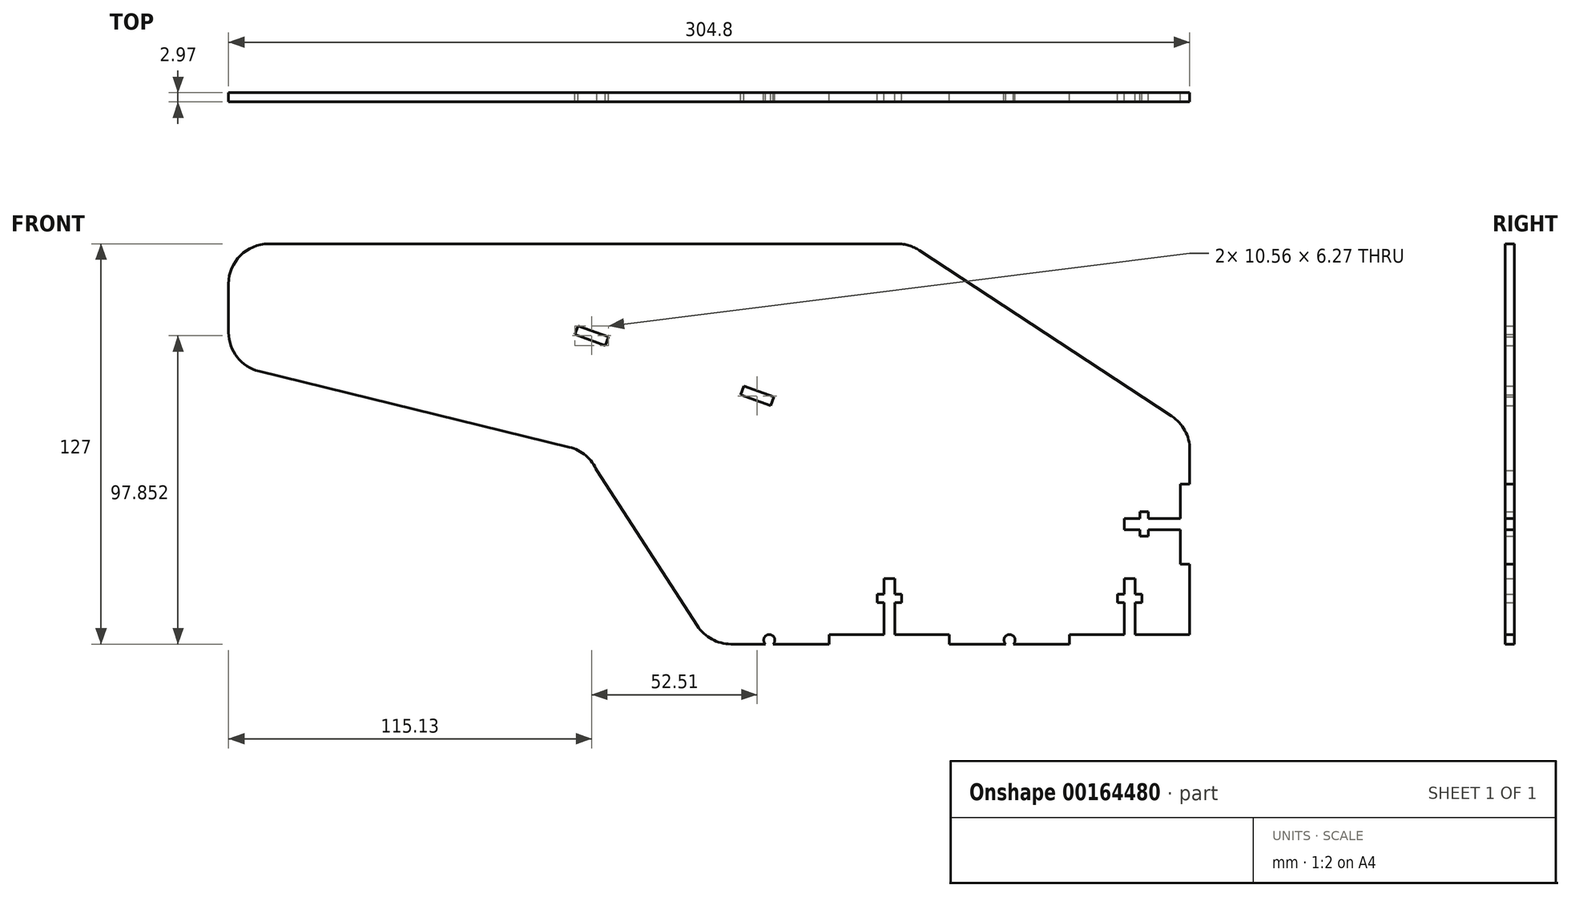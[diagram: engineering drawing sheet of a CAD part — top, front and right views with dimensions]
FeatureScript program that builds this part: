
annotation { "Feature Type Name" : "Feature", "Feature Type Description" : "" }
export const myFeature = defineFeature(function(context is Context, id is Id, definition is map)
    precondition{}
    {
        {
            var Q0;
            Q0=qCreatedBy(makeId("Front.planeOp"),FACE);
            var sketch = newSketch(context, id + "F0", { "sketchPlane" : qUnion([Q0])});
            skLineSegment(sketch, "E0.bottom", {"start": v(152.4, -63.5) * mm, "end": v(17.8, -63.5) * mm});
            skLineSegment(sketch, "E0.top", {"start": v(59.7, 63.5) * mm, "end": v(-139.7, 63.5) * mm});
            skLineSegment(sketch, "E0.left", {"start": v(152.4, -63.5) * mm, "end": v(152.4, -1.77) * mm});
            skLineSegment(sketch, "E0.right", {"start": v(-152.4, 35.37) * mm, "end": v(-152.4, 50.8) * mm});
            skPoint(sketch, "E0.middle", {"position": v(0, 0) * mm});
            skPoint(sketch, "E1", {"position": v(-152.4, 25.4) * mm});
            skPoint(sketch, "E2.orphan", {"position": v(-152.4, -63.5) * mm});
            skLineSegment(sketch, "E3.bottom", {"start": v(38.1, -60.53) * mm, "end": v(55.38, -60.53) * mm});
            skLineSegment(sketch, "E3.top", {"start": v(38.1, -63.5) * mm, "end": v(76.2, -63.5) * mm});
            skLineSegment(sketch, "E3.left", {"start": v(38.1, -60.53) * mm, "end": v(38.1, -63.5) * mm});
            skLineSegment(sketch, "E3.right", {"start": v(76.2, -60.53) * mm, "end": v(76.2, -63.5) * mm});
            skLineSegment(sketch, "E4.bottom", {"start": v(55.38, -42.7) * mm, "end": v(58.92, -42.7) * mm});
            skLineSegment(sketch, "E4.top", {"start": v(55.38, -63.5) * mm, "end": v(58.92, -63.5) * mm});
            skLineSegment(sketch, "E4.left", {"start": v(55.38, -42.7) * mm, "end": v(55.38, -47.73) * mm});
            skLineSegment(sketch, "E4.right", {"start": v(58.92, -42.7) * mm, "end": v(58.92, -47.73) * mm});
            skPoint(sketch, "E5", {"position": v(57.15, -63.5) * mm});
            skLineSegment(sketch, "E6", {"start": v(57.15, -63.5) * mm, "end": v(57.15, -38.1) * mm, "construction": true});
            skPoint(sketch, "E6.endSnap0", {"position": v(57.15, -42.7) * mm});
            skLineSegment(sketch, "E7.bottom", {"start": v(61.04, -50.37) * mm, "end": v(58.92, -50.37) * mm});
            skLineSegment(sketch, "E7.top", {"start": v(61.04, -47.73) * mm, "end": v(58.92, -47.73) * mm});
            skLineSegment(sketch, "E7.left", {"start": v(61.04, -50.37) * mm, "end": v(61.04, -47.73) * mm});
            skLineSegment(sketch, "E7.right", {"start": v(53.26, -50.37) * mm, "end": v(53.26, -47.73) * mm});
            skPoint(sketch, "E7.middle", {"position": v(57.15, -49.05) * mm});
            skLineSegment(sketch, "E8.trimOffspring", {"start": v(58.92, -60.53) * mm, "end": v(76.2, -60.53) * mm});
            skLineSegment(sketch, "E9.trimOffspring", {"start": v(58.92, -50.37) * mm, "end": v(58.92, -60.53) * mm});
            skLineSegment(sketch, "E10.trimOffspring", {"start": v(55.38, -50.37) * mm, "end": v(55.38, -60.53) * mm});
            skLineSegment(sketch, "E11.trimOffspring", {"start": v(55.38, -47.73) * mm, "end": v(53.26, -47.73) * mm});
            skLineSegment(sketch, "E12.trimOffspring", {"start": v(55.38, -50.37) * mm, "end": v(53.26, -50.37) * mm});
            skArc(sketch, "E13", {"start": v(20.3, -63.5) * mm, "mid": v(19.05, -60.45) * mm, "end": v(17.8, -63.5) * mm});
            skLineSegment(sketch, "E14.1.0.0", {"start": v(133.35, -63.5) * mm, "end": v(133.35, -38.1) * mm, "construction": true});
            skLineSegment(sketch, "E14.1.0.1", {"start": v(131.58, -50.37) * mm, "end": v(131.58, -60.53) * mm});
            skPoint(sketch, "E14.1.0.2", {"position": v(133.35, -42.7) * mm});
            skPoint(sketch, "E14.1.0.3", {"position": v(133.35, -63.5) * mm});
            skLineSegment(sketch, "E14.1.0.4", {"start": v(114.3, -60.53) * mm, "end": v(131.58, -60.53) * mm});
            skLineSegment(sketch, "E14.1.0.5", {"start": v(114.3, -63.5) * mm, "end": v(152.4, -63.5) * mm});
            skLineSegment(sketch, "E14.1.0.6", {"start": v(135.12, -50.37) * mm, "end": v(135.12, -60.53) * mm});
            skLineSegment(sketch, "E14.1.0.7", {"start": v(135.12, -60.53) * mm, "end": v(152.4, -60.53) * mm});
            skPoint(sketch, "E14.1.0.8", {"position": v(133.35, -49.05) * mm});
            skArc(sketch, "E14.1.0.9", {"start": v(96.5, -63.5) * mm, "mid": v(95.25, -60.45) * mm, "end": v(94, -63.5) * mm});
            skLineSegment(sketch, "E14.1.0.10", {"start": v(135.12, -42.7) * mm, "end": v(135.12, -47.73) * mm});
            skLineSegment(sketch, "E14.1.0.11", {"start": v(114.3, -60.53) * mm, "end": v(114.3, -63.5) * mm});
            skLineSegment(sketch, "E14.1.0.12", {"start": v(152.4, -60.53) * mm, "end": v(152.4, -63.5) * mm});
            skLineSegment(sketch, "E14.1.0.13", {"start": v(137.24, -47.73) * mm, "end": v(135.12, -47.73) * mm});
            skLineSegment(sketch, "E14.1.0.14", {"start": v(131.58, -63.5) * mm, "end": v(135.12, -63.5) * mm});
            skLineSegment(sketch, "E14.1.0.15", {"start": v(131.58, -47.73) * mm, "end": v(129.46, -47.73) * mm});
            skLineSegment(sketch, "E14.1.0.16", {"start": v(131.58, -42.7) * mm, "end": v(131.58, -47.73) * mm});
            skLineSegment(sketch, "E14.1.0.17", {"start": v(131.58, -42.7) * mm, "end": v(135.12, -42.7) * mm});
            skLineSegment(sketch, "E14.1.0.18", {"start": v(137.24, -50.37) * mm, "end": v(135.12, -50.37) * mm});
            skLineSegment(sketch, "E14.1.0.19", {"start": v(137.24, -50.37) * mm, "end": v(137.24, -47.73) * mm});
            skLineSegment(sketch, "E14.1.0.20", {"start": v(131.58, -50.37) * mm, "end": v(129.46, -50.37) * mm});
            skLineSegment(sketch, "E14.1.0.21", {"start": v(129.46, -50.37) * mm, "end": v(129.46, -47.73) * mm});
            skLineSegment(sketch, "E14.direction1", {"start": v(17.8, -63.5) * mm, "end": v(94, -63.5) * mm, "construction": true});
            skPoint(sketch, "E15.visualSharp", {"position": v(-152.4, 63.5) * mm});
            skArc(sketch, "E15.filletArc", {"start": v(-139.7, 63.5) * mm, "mid": v(-148.68, 59.78) * mm, "end": v(-152.4, 50.8) * mm});
            skLineSegment(sketch, "E16", {"start": v(-142.72, 23.03) * mm, "end": v(-44.34, -1.02) * mm});
            skArc(sketch, "E17.filletArc", {"start": v(-152.4, 35.37) * mm, "mid": v(-149.69, 27.53) * mm, "end": v(-142.72, 23.03) * mm});
            skArc(sketch, "E18.filletArc", {"start": v(-35.63, -8.47) * mm, "mid": v(-39.1, -3.7) * mm, "end": v(-44.34, -1.02) * mm});
            skPoint(sketch, "E19.visualSharp", {"position": v(-12.7, -63.5) * mm});
            skPoint(sketch, "E20", {"position": v(63.5, 63.5) * mm});
            skPoint(sketch, "E21", {"position": v(152.4, 5.08) * mm});
            skLineSegment(sketch, "E22", {"start": v(66.68, 61.41) * mm, "end": v(146.67, 8.84) * mm});
            skArc(sketch, "E23.filletArc", {"start": v(66.68, 61.41) * mm, "mid": v(63.34, 62.97) * mm, "end": v(59.7, 63.5) * mm});
            skArc(sketch, "E24.filletArc", {"start": v(152.4, -1.77) * mm, "mid": v(150.88, 4.26) * mm, "end": v(146.67, 8.84) * mm});
            skPoint(sketch, "E25", {"position": v(0, -63.49) * mm});
            skLineSegment(sketch, "E26", {"start": v(-35.63, -8.47) * mm, "end": v(-3.75, -57.7) * mm});
            skLineSegment(sketch, "E27", {"start": v(6.9, -63.5) * mm, "end": v(17.8, -63.5) * mm});
            skArc(sketch, "E28.filletArc", {"start": v(-3.75, -57.7) * mm, "mid": v(0.84, -61.95) * mm, "end": v(6.9, -63.5) * mm});
            skLineSegment(sketch, "E29.bottom", {"start": v(152.4, -12.7) * mm, "end": v(149.43, -12.7) * mm});
            skLineSegment(sketch, "E29.top", {"start": v(152.4, -38.1) * mm, "end": v(149.43, -38.1) * mm});
            skLineSegment(sketch, "E29.left", {"start": v(152.4, -12.7) * mm, "end": v(152.4, -38.1) * mm});
            skLineSegment(sketch, "E29.right", {"start": v(149.43, -12.7) * mm, "end": v(149.43, -23.63) * mm});
            skLineSegment(sketch, "E30.bottom", {"start": v(131.6, -23.63) * mm, "end": v(136.63, -23.63) * mm});
            skLineSegment(sketch, "E30.top", {"start": v(131.6, -27.17) * mm, "end": v(136.63, -27.17) * mm});
            skLineSegment(sketch, "E30.left", {"start": v(131.6, -23.63) * mm, "end": v(131.6, -27.17) * mm});
            skLineSegment(sketch, "E30.right", {"start": v(152.4, -23.63) * mm, "end": v(152.4, -27.17) * mm});
            skPoint(sketch, "E31", {"position": v(152.4, -25.4) * mm});
            skLineSegment(sketch, "E32", {"start": v(152.4, -25.4) * mm, "end": v(121.92, -25.4) * mm, "construction": true});
            skPoint(sketch, "E32.endSnap0", {"position": v(131.6, -25.4) * mm});
            skLineSegment(sketch, "E33.bottom", {"start": v(139.27, -29.29) * mm, "end": v(136.63, -29.29) * mm});
            skLineSegment(sketch, "E33.top", {"start": v(139.27, -21.51) * mm, "end": v(136.63, -21.51) * mm});
            skLineSegment(sketch, "E33.left", {"start": v(139.27, -29.29) * mm, "end": v(139.27, -27.17) * mm});
            skLineSegment(sketch, "E33.right", {"start": v(136.63, -29.29) * mm, "end": v(136.63, -27.17) * mm});
            skPoint(sketch, "E33.middle", {"position": v(137.95, -25.4) * mm});
            skLineSegment(sketch, "E34.trimOffspring", {"start": v(149.43, -27.17) * mm, "end": v(149.43, -38.1) * mm});
            skLineSegment(sketch, "E35.trimOffspring", {"start": v(139.27, -23.63) * mm, "end": v(139.27, -21.51) * mm});
            skLineSegment(sketch, "E36.trimOffspring", {"start": v(139.27, -27.17) * mm, "end": v(149.43, -27.17) * mm});
            skLineSegment(sketch, "E37.trimOffspring", {"start": v(136.63, -23.63) * mm, "end": v(136.63, -21.51) * mm});
            skLineSegment(sketch, "E38.trimOffspring", {"start": v(139.27, -23.63) * mm, "end": v(149.43, -23.63) * mm});
            skLineSegment(sketch, "E39.bottom", {"start": v(19.5, 12.1) * mm, "end": v(9.96, 15.58) * mm});
            skLineSegment(sketch, "E39.top", {"start": v(20.52, 14.9) * mm, "end": v(10.97, 18.37) * mm});
            skLineSegment(sketch, "E39.left", {"start": v(19.5, 12.1) * mm, "end": v(20.52, 14.9) * mm});
            skLineSegment(sketch, "E39.right", {"start": v(9.96, 15.58) * mm, "end": v(10.97, 18.37) * mm});
            skPoint(sketch, "E39.middle", {"position": v(15.24, 15.24) * mm});
            skLineSegment(sketch, "E40", {"start": v(15.24, 15.24) * mm, "end": v(-52.5, 39.9) * mm, "construction": true});
            skLineSegment(sketch, "E41.bottom", {"start": v(-33, 31.22) * mm, "end": v(-42.55, 34.7) * mm});
            skLineSegment(sketch, "E41.top", {"start": v(-31.99, 34.01) * mm, "end": v(-41.54, 37.49) * mm});
            skLineSegment(sketch, "E41.left", {"start": v(-33, 31.22) * mm, "end": v(-31.99, 34.01) * mm});
            skLineSegment(sketch, "E41.right", {"start": v(-42.55, 34.7) * mm, "end": v(-41.54, 37.49) * mm});
            skPoint(sketch, "E41.middle", {"position": v(-37.27, 34.35) * mm});
            skSolve(sketch);
        }
        {
            var Q0;
            Q0=makeQuery(id+"F0.imprint","IMPRINT",FACE,{"disambiguationData":[TD([[makeQuery(id+"F0.imprint","IMPRINT",EDGE,{"derivedFrom":sQuery(id+"F0.wireOp",EDGE,"E0.top")}),1.0]])]});
            extrude(context, id + "F1", {"entities" : qUnion([Q0]), "depth" : 2.97 * mm});
        }
    });
